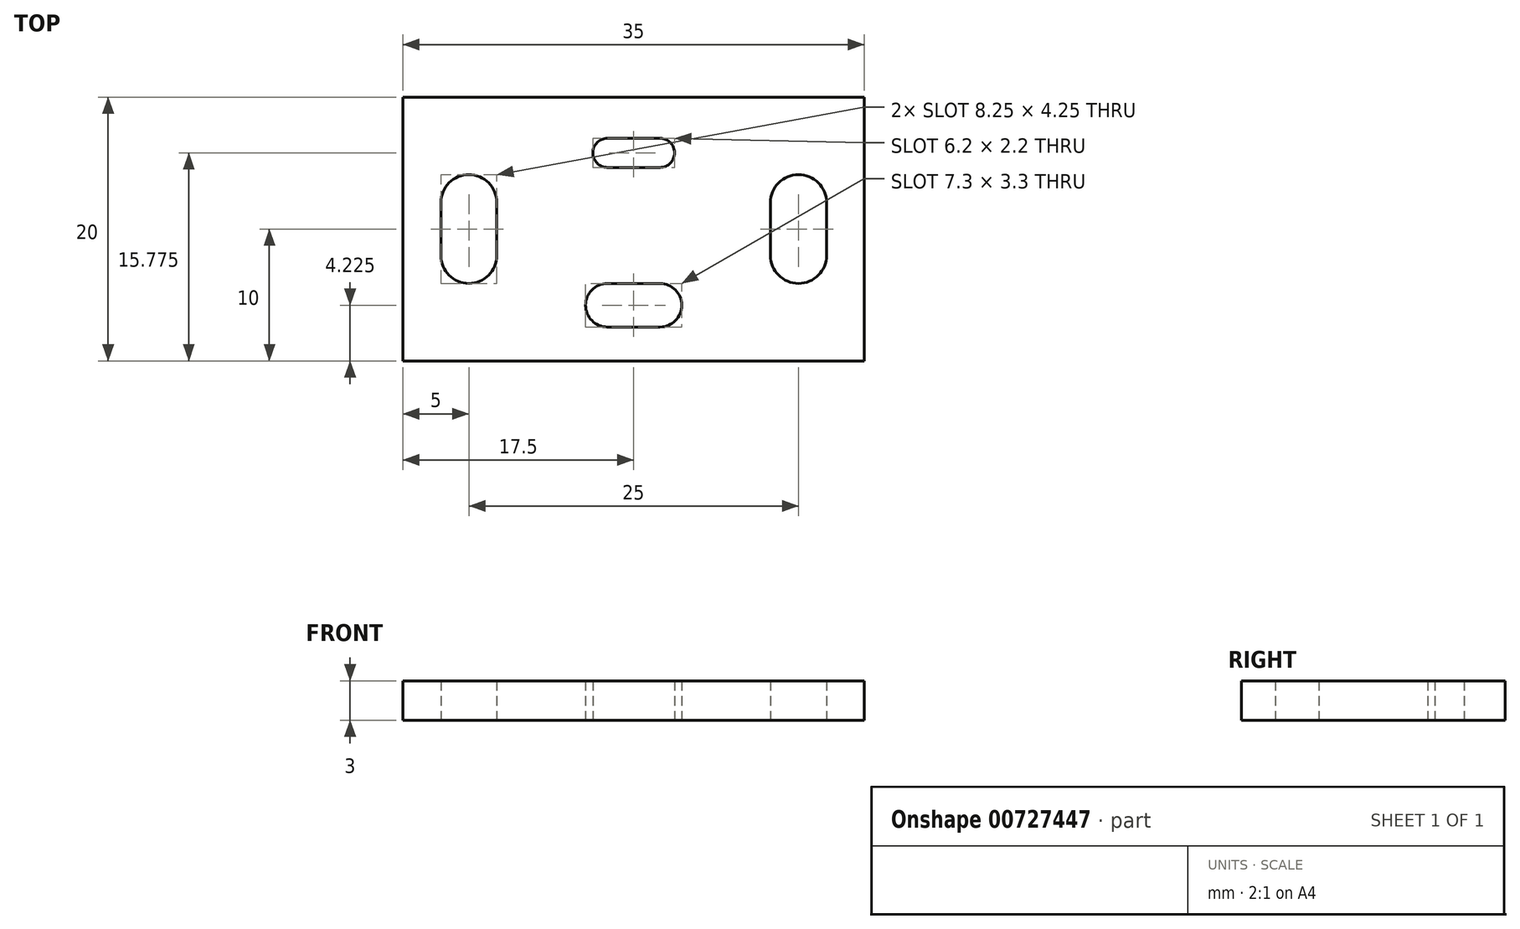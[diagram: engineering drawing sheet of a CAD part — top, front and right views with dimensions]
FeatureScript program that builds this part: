
annotation { "Feature Type Name" : "Feature", "Feature Type Description" : "" }
export const myFeature = defineFeature(function(context is Context, id is Id, definition is map)
    precondition{}
    {
        {
            var Q0;
            Q0=qCreatedBy(makeId("Top.planeOp"),FACE);
            var sketch = newSketch(context, id + "F0", { "sketchPlane" : qUnion([Q0])});
            skLineSegment(sketch, "E0.bottom", {"start": v(17.5, -10) * mm, "end": v(-17.5, -10) * mm});
            skLineSegment(sketch, "E0.top", {"start": v(17.5, 10) * mm, "end": v(-17.5, 10) * mm});
            skLineSegment(sketch, "E0.left", {"start": v(17.5, -10) * mm, "end": v(17.5, 10) * mm});
            skLineSegment(sketch, "E0.right", {"start": v(-17.5, -10) * mm, "end": v(-17.5, 10) * mm});
            skPoint(sketch, "E0.middle", {"position": v(0, 0) * mm});
            skLineSegment(sketch, "E1", {"start": v(-17.5, 5.78) * mm, "end": v(17.5, 5.77) * mm, "construction": true});
            skLineSegment(sketch, "E2", {"start": v(-17.5, -5.77) * mm, "end": v(17.5, -5.78) * mm, "construction": true});
            skLineSegment(sketch, "E3", {"start": v(-12.5, 10) * mm, "end": v(-12.5, -10) * mm, "construction": true});
            skLineSegment(sketch, "E4", {"start": v(12.5, 10) * mm, "end": v(12.5, -10) * mm, "construction": true});
            skArc(sketch, "E5", {"start": v(-10.38, 2) * mm, "mid": v(-12.5, 4.12) * mm, "end": v(-14.62, 2) * mm});
            skArc(sketch, "E6", {"start": v(-10.38, -2) * mm, "mid": v(-12.5, -4.12) * mm, "end": v(-14.62, -2) * mm});
            skLineSegment(sketch, "E7", {"start": v(-10.38, 2) * mm, "end": v(-10.37, -2) * mm});
            skLineSegment(sketch, "E8", {"start": v(-14.62, 2) * mm, "end": v(-14.62, -2) * mm});
            skArc(sketch, "E9", {"start": v(14.62, -2) * mm, "mid": v(12.5, -4.12) * mm, "end": v(10.38, -2) * mm});
            skArc(sketch, "E10", {"start": v(10.38, 2) * mm, "mid": v(12.5, 4.12) * mm, "end": v(14.62, 2) * mm});
            skLineSegment(sketch, "E11", {"start": v(10.38, -2) * mm, "end": v(10.38, 2) * mm});
            skLineSegment(sketch, "E12", {"start": v(14.62, 2) * mm, "end": v(14.62, -2) * mm});
            skArc(sketch, "E13", {"start": v(-2, 6.88) * mm, "mid": v(-3.1, 5.78) * mm, "end": v(-2, 4.68) * mm});
            skArc(sketch, "E14", {"start": v(2, 6.88) * mm, "mid": v(3.1, 5.78) * mm, "end": v(2, 4.68) * mm});
            skLineSegment(sketch, "E15", {"start": v(-2, 6.88) * mm, "end": v(2, 6.88) * mm});
            skLineSegment(sketch, "E16", {"start": v(2, 4.68) * mm, "end": v(-2, 4.67) * mm});
            skArc(sketch, "E17", {"start": v(-2, -4.12) * mm, "mid": v(-3.65, -5.78) * mm, "end": v(-2, -7.43) * mm});
            skArc(sketch, "E18", {"start": v(2, -4.12) * mm, "mid": v(3.65, -5.78) * mm, "end": v(2, -7.43) * mm});
            skLineSegment(sketch, "E19", {"start": v(-2, -4.12) * mm, "end": v(2, -4.12) * mm});
            skLineSegment(sketch, "E20", {"start": v(2, -7.42) * mm, "end": v(-2, -7.43) * mm});
            skSolve(sketch);
        }
        {
            var Q0;
            Q0 = qSketchRegion(id + "F0", true);
            extrude(context, id + "F1", {"entities" : qUnion([Q0]), "depth" : 3 * mm, "offsetDistance" : 25 * mm});
        }
    });
